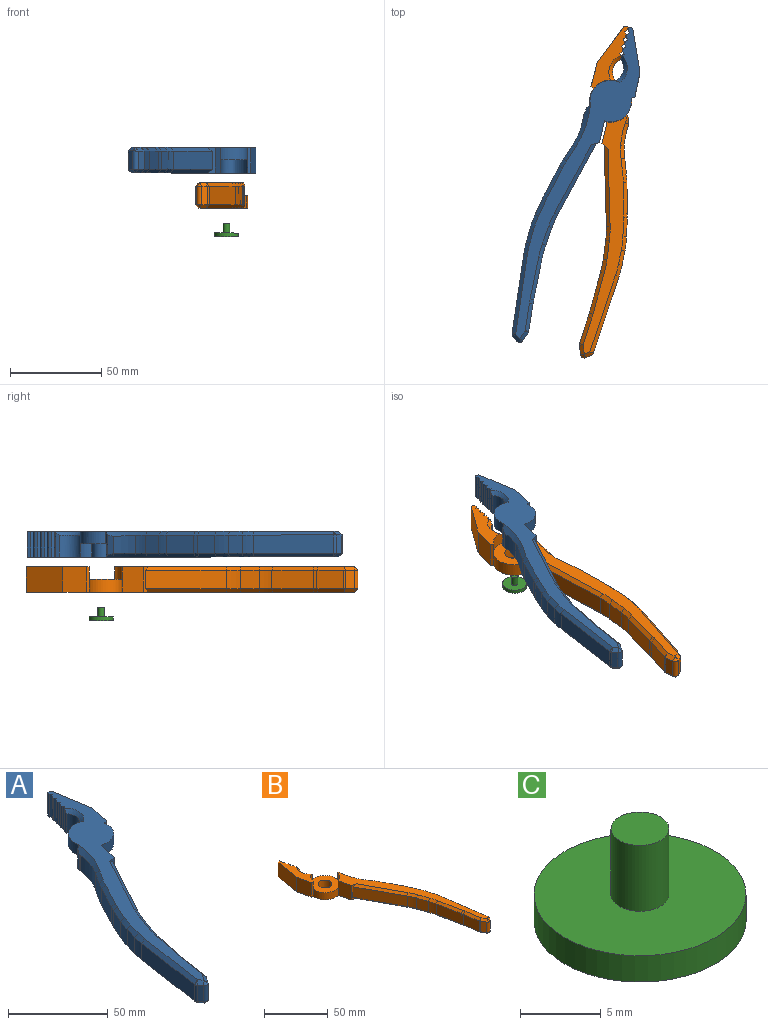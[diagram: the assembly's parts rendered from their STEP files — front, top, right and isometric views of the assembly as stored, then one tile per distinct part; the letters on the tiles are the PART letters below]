
ASSEMBLY  parts=3 mates=3
PART A: 110 faces, bbox 70.2x172.9x14.1 mm
  f0: plane 127.45x48.58mm, normal (0,0,-1), area 866.7mm2, adj f19,f22,f36,f43,f58,f59,f60,f61
  f1: plane 14x1.82mm, normal (-0.97,0.25,0), area 26.3mm2, adj f3,f5,f11,f12
  f2: plane 14x1.29mm, normal (-0.51,0.86,0), area 21mm2, adj f3,f11,f12,f13,f109
  f3: plane 14x1.29mm, normal (-0.86,-0.51,0), area 21mm2, adj f1,f2,f11,f12
  f4: plane 14x1.82mm, normal (-0.97,0.25,0), area 26.3mm2, adj f6,f8,f11,f12
  f5: plane 14x1.29mm, normal (-0.51,0.86,0), area 21mm2, adj f1,f6,f11,f12
  f6: plane 14x1.29mm, normal (-0.86,-0.51,0), area 21mm2, adj f4,f5,f11,f12
  f7: plane 14x1.82mm, normal (-0.97,0.25,0), area 26.3mm2, adj f9,f11,f12,f105
  f8: plane 14x1.29mm, normal (-0.51,0.86,0), area 21mm2, adj f4,f9,f11,f12
  f9: plane 14x1.29mm, normal (-0.86,-0.51,0), area 21mm2, adj f7,f8,f11,f12
  f10: plane 14x1.94mm, normal (-0.97,0.25,0), area 28mm2, adj f11,f12,f41,f106
  f11: plane 170.82x68.11mm, normal (0,0,1), area 1516.7mm2, adj f1,f2,f3,f4,f5,f6,f7,f8
  f12: plane 38.87x13mm, normal (0,0,-1), area 250.2mm2, adj f1,f2,f3,f4,f5,f6,f7,f8
  f13: plane 13.83x2.12mm, normal (-0.97,0.25,0), area 28.2mm2, adj f2,f12,f104,f109
  f14: plane 23.11x22.77mm, normal (0,0,-1), area 337.5mm2, adj f15,f16,f18,f19,f20,f21,f22,f37
  f15: cylinder r=11.39mm len=14.76mm, axis (0,0,1), area 150.8mm2, adj f11,f14,f20,f37
  f16: cylinder r=5.05mm len=10.1mm, axis (0,0,-1), area 234.7mm2, adj f14,f17
  f17: plane 10.1x10.1mm, normal (0,0,-1), area 67.5mm2, adj f16,f44
  f18: cylinder r=11.39mm len=16.38mm, axis (0,0,1), area 154.8mm2, adj f11,f14,f21,f104,f109
  f19: plane 14x11.63mm, normal (0.97,-0.23,0), area 165.9mm2, adj f0,f11,f14,f20,f36,f43
  f20: plane 6.6x0.19mm, normal (0.94,-0.34,0), area 1.3mm2, adj f11,f14,f15,f19
  f21: plane 6.6x0.19mm, normal (-0.35,0.94,0), area 1.3mm2, adj f11,f14,f18,f22,f82
  f22: plane 13.91x1.76mm, normal (-0.47,0.88,0), area 23.7mm2, adj f0,f14,f21,f23,f43,f78,f82
  f23: plane 11.38x3.12mm, normal (-0.9,0.44,0), area 34.7mm2, adj f22,f24,f78,f82
  f24: plane 9.32x0.14mm, normal (-0.99,0.15,0), area 1.3mm2, adj f23,f50,f78,f82
  f25: plane 10x7.38mm, normal (-0.84,0.55,0), area 88.1mm2, adj f49,f51,f79,f83
  f26: plane 14.93x10mm, normal (-0.89,0.46,0), area 168.5mm2, adj f51,f52,f76,f85
  f27: plane 10x9.39mm, normal (-0.91,0.42,0), area 103.4mm2, adj f52,f53,f74,f87
  f28: plane 10x7.47mm, normal (-0.96,0.27,0), area 77.5mm2, adj f53,f54,f72,f89
  f29: plane 43.91x10mm, normal (-0.99,0.15,0), area 443.9mm2, adj f46,f54,f70,f91
  f30: plane 10x2.64mm, normal (-0.78,-0.62,0), area 33.8mm2, adj f46,f47,f68,f93
  f31: plane 10x4.35mm, normal (0.82,-0.57,0), area 53mm2, adj f47,f48,f66,f95
  f32: plane 15.18x10mm, normal (0.99,-0.15,0), area 153.7mm2, adj f48,f55,f64,f97
  f33: plane 22.93x10mm, normal (0.98,-0.2,0), area 233.9mm2, adj f55,f56,f62,f99
  f34: plane 10x9.8mm, normal (0.94,-0.34,0), area 104mm2, adj f56,f57,f60,f101
  f35: plane 39.02x21.16mm, normal (0.88,-0.48,0), area 443.9mm2, adj f36,f57,f58,f103
  f36: plane 14x4.33mm, normal (0.28,-0.96,0), area 29.3mm2, adj f0,f11,f19,f35,f58,f103
  f37: plane 6.6x0.19mm, normal (0.5,-0.87,0), area 1.4mm2, adj f11,f14,f15,f38
  f38: plane 14x1.78mm, normal (0.32,-0.95,0), area 24.8mm2, adj f11,f12,f14,f37,f39,f42
  f39: plane 14x13.16mm, normal (0.98,-0.21,0), area 188.4mm2, adj f11,f12,f38,f40
  f40: plane 24.65x14mm, normal (0.99,0.16,0), area 349.4mm2, adj f11,f12,f39,f41
  f41: plane 14x2.04mm, normal (0.25,0.97,0), area 29.5mm2, adj f10,f11,f12,f40
  f42: cylinder r=11.79mm len=9.67mm, axis (0,0,1), area 101.5mm2, adj f12,f14,f38,f104
  f43: cylinder r=11.79mm len=8.46mm, axis (0,0,1), area 89.9mm2, adj f0,f14,f19,f22
  f44: cylinder r=2mm len=9mm, axis (0,0,-1), area 113.1mm2, adj f17,f45
  f45: plane 4x4mm, normal (0,0,-1), area 12.6mm2, adj f44
  f46: cylinder r=2mm len=10mm, axis (0,0,-1), area 16.4mm2, adj f29,f30,f69,f92
  f47: cylinder r=2mm len=10mm, axis (0,0,-1), area 37.2mm2, adj f30,f31,f67,f94
  f48: cylinder r=2mm len=10mm, axis (0,0,-1), area 9mm2, adj f31,f32,f65,f96
  f49: cylinder r=50mm len=10mm, axis (0,0,1), area 64.9mm2, adj f25,f50,f81,f82
  f50: cylinder r=50mm len=11.8mm, axis (0,0,1), area 118.5mm2, adj f24,f49,f80,f82
  f51: cylinder r=50mm len=10mm, axis (0,0,-1), area 47.7mm2, adj f25,f26,f77,f84
  f52: cylinder r=50mm len=10mm, axis (0,0,-1), area 25.6mm2, adj f26,f27,f75,f86
  f53: cylinder r=50mm len=10mm, axis (0,0,-1), area 79.7mm2, adj f27,f28,f73,f88
  f54: cylinder r=50mm len=10mm, axis (0,0,-1), area 62.4mm2, adj f28,f29,f71,f90
  f55: cylinder r=50mm len=10mm, axis (0,0,1), area 22.1mm2, adj f32,f33,f63,f98
  f56: cylinder r=50mm len=10mm, axis (0,0,1), area 71.2mm2, adj f33,f34,f61,f100
  f57: cylinder r=50mm len=10mm, axis (0,0,1), area 77.5mm2, adj f34,f35,f59,f102
  f58: plane 39.02x22.92mm, normal (0.62,-0.34,-0.71), area 122.7mm2, adj f0,f35,f36,f59
  f59: cone r=52mm half-angle=45deg, axis (0,0,-1), area 22.4mm2, adj f0,f57,f58,f60
  f60: plane 10.47x5.37mm, normal (0.67,-0.24,-0.71), area 29.4mm2, adj f0,f34,f59,f61
  f61: cone r=52mm half-angle=45deg, axis (0,0,-1), area 20.5mm2, adj f0,f56,f60,f62
  f62: plane 23.32x6.6mm, normal (0.69,-0.14,-0.71), area 66.2mm2, adj f0,f33,f61,f63
  f63: cone r=52mm half-angle=45deg, axis (0,0,-1), area 6.4mm2, adj f0,f55,f62,f64
  f64: plane 15.49x4.35mm, normal (0.7,-0.11,-0.71), area 43.5mm2, adj f0,f32,f63,f65
  f65: cone r=2mm half-angle=45deg, axis (0,0,1), area 1.3mm2, adj f48,f64,f66
  f66: plane 5.49x4.67mm, normal (0.58,-0.4,-0.71), area 15mm2, adj f0,f31,f65,f67
  f67: cone r=2mm half-angle=45deg, axis (0,0,1), area 5.3mm2, adj f47,f66,f68
  f68: plane 3.89x3.67mm, normal (-0.55,-0.44,-0.71), area 9.6mm2, adj f0,f30,f67,f69
  f69: cone r=2mm half-angle=45deg, axis (0,0,1), area 2.3mm2, adj f46,f68,f70
  f70: plane 44.21x8.48mm, normal (-0.7,0.1,-0.71), area 125.6mm2, adj f0,f29,f69,f71
  f71: cone r=48mm half-angle=45deg, axis (0,0,1), area 17.3mm2, adj f0,f54,f70,f72
  f72: plane 8.01x4.01mm, normal (-0.68,0.19,-0.71), area 21.9mm2, adj f0,f28,f71,f73
  f73: cone r=48mm half-angle=45deg, axis (0,0,1), area 22.1mm2, adj f0,f53,f72,f74
  f74: plane 10.23x6.14mm, normal (-0.64,0.3,-0.71), area 29.2mm2, adj f0,f27,f73,f75
  f75: cone r=48mm half-angle=45deg, axis (0,0,1), area 7.1mm2, adj f0,f52,f74,f76
  f76: plane 15.86x9.59mm, normal (-0.63,0.33,-0.71), area 47.7mm2, adj f0,f26,f75,f77
  f77: cone r=48mm half-angle=45deg, axis (0,0,1), area 13.2mm2, adj f0,f51,f76,f79
  f78: plane 4.04x2.58mm, normal (-0.7,0.1,-0.71), area 7.7mm2, adj f0,f22,f23,f24,f80
  f79: plane 8.47x6.49mm, normal (-0.59,0.39,-0.71), area 24.9mm2, adj f0,f25,f77,f81
  f80: cone r=52mm half-angle=45deg, axis (0,0,-1), area 35.5mm2, adj f0,f50,f78,f81
  f81: cone r=52mm half-angle=45deg, axis (0,0,-1), area 18.8mm2, adj f0,f49,f79,f80
  f82: cone r=50mm half-angle=45deg, axis (0,0,1), area 72.5mm2, adj f11,f21,f22,f23,f24,f49,f50,f83
  f83: plane 8.47x6.49mm, normal (-0.59,0.39,0.71), area 24.9mm2, adj f11,f25,f82,f84
  f84: cone r=48mm half-angle=45deg, axis (0,0,-1), area 13.2mm2, adj f11,f51,f83,f85
  f85: plane 15.86x9.59mm, normal (-0.63,0.33,0.71), area 47.7mm2, adj f11,f26,f84,f86
  f86: cone r=48mm half-angle=45deg, axis (0,0,-1), area 7.1mm2, adj f11,f52,f85,f87
  f87: plane 10.23x6.14mm, normal (-0.64,0.3,0.71), area 29.2mm2, adj f11,f27,f86,f88
  f88: cone r=48mm half-angle=45deg, axis (0,0,-1), area 22.1mm2, adj f11,f53,f87,f89
  f89: plane 8.01x4.01mm, normal (-0.68,0.19,0.71), area 21.9mm2, adj f11,f28,f88,f90
  f90: cone r=48mm half-angle=45deg, axis (0,0,-1), area 17.3mm2, adj f11,f54,f89,f91
  f91: plane 44.21x8.48mm, normal (-0.7,0.1,0.71), area 125.6mm2, adj f11,f29,f90,f92
  f92: cone r=2mm half-angle=45deg, axis (0,0,-1), area 2.3mm2, adj f46,f91,f93
  f93: plane 3.89x3.67mm, normal (-0.55,-0.44,0.71), area 9.6mm2, adj f11,f30,f92,f94
  f94: cone r=2mm half-angle=45deg, axis (0,0,-1), area 5.3mm2, adj f47,f93,f95
  f95: plane 5.49x4.67mm, normal (0.58,-0.4,0.71), area 15mm2, adj f11,f31,f94,f96
  f96: cone r=2mm half-angle=45deg, axis (0,0,-1), area 1.3mm2, adj f48,f95,f97
  f97: plane 15.49x4.35mm, normal (0.7,-0.11,0.71), area 43.5mm2, adj f11,f32,f96,f98
  f98: cone r=52mm half-angle=45deg, axis (0,0,1), area 6.4mm2, adj f11,f55,f97,f99
  f99: plane 23.32x6.6mm, normal (0.69,-0.14,0.71), area 66.2mm2, adj f11,f33,f98,f100
  f100: cone r=52mm half-angle=45deg, axis (0,0,1), area 20.5mm2, adj f11,f56,f99,f101
  f101: plane 10.47x5.37mm, normal (0.67,-0.24,0.71), area 29.4mm2, adj f11,f34,f100,f102
  f102: cone r=52mm half-angle=45deg, axis (0,0,1), area 22.4mm2, adj f11,f57,f101,f103
  f103: plane 39.02x22.92mm, normal (0.62,-0.34,0.71), area 122.7mm2, adj f11,f35,f36,f102
  f104: cylinder r=7.62mm len=12mm, axis (0,0,1), area 163.4mm2, adj f12,f13,f14,f18,f42,f109
  f105: plane 14x1.29mm, normal (-0.51,0.86,0), area 21mm2, adj f7,f11,f12,f106
  f106: plane 14x1.29mm, normal (-0.86,-0.51,0), area 21mm2, adj f10,f11,f12,f105
  f107: extruded ~7.78x5.87mm, area 30.5mm2, adj f0,f108
  f108: plane 7.97x6.05mm, normal (0,0,-1), area 20.7mm2, adj f107
  f109: cone r=7.62mm half-angle=45deg, axis (0,0,1), area 43.8mm2, adj f2,f11,f13,f18,f104
PART B: 122 faces, bbox 70.1x172.8x14 mm
  f0: plane 170.82x68.11mm, normal (0,0,-1), area 1434.8mm2, adj f1,f2,f3,f4,f5,f6,f7,f8
  f1: plane 14x1.82mm, normal (0.97,0.25,0), area 26.3mm2, adj f0,f2,f6,f24
  f2: plane 14x1.29mm, normal (0.86,-0.51,0), area 21mm2, adj f0,f1,f3,f24
  f3: plane 14x1.29mm, normal (0.51,0.86,0), area 21mm2, adj f0,f2,f11,f24,f121
  f4: plane 14x1.82mm, normal (0.97,0.25,0), area 26.3mm2, adj f0,f5,f9,f24
  f5: plane 14x1.29mm, normal (0.86,-0.51,0), area 21mm2, adj f0,f4,f6,f24
  f6: plane 14x1.29mm, normal (0.51,0.86,0), area 21mm2, adj f0,f1,f5,f24
  f7: plane 14x1.82mm, normal (0.97,0.25,0), area 26.3mm2, adj f0,f8,f24,f108
  f8: plane 14x1.29mm, normal (0.86,-0.51,0), area 21mm2, adj f0,f7,f9,f24
  f9: plane 14x1.29mm, normal (0.51,0.86,0), area 21mm2, adj f0,f4,f8,f24
  f10: plane 14x1.94mm, normal (0.97,0.25,0), area 28mm2, adj f0,f21,f24,f107
  f11: plane 13.83x2.12mm, normal (0.97,0.25,0), area 28.2mm2, adj f0,f3,f104,f121
  f12: cylinder r=11.59mm len=7mm, axis (0,0,-1), area 35.6mm2, adj f0,f13,f103,f105
  f13: plane 23.17x23.17mm, normal (0,0,1), area 328.4mm2, adj f12,f14,f15,f16,f17,f18,f19,f25
  f14: cylinder r=11.59mm len=9.6mm, axis (0,0,-1), area 93.5mm2, adj f13,f20,f24,f104,f121
  f15: cylinder r=11.59mm len=15.03mm, axis (0,0,-1), area 163.4mm2, adj f0,f13,f20,f27
  f16: cylinder r=11.59mm len=9.6mm, axis (0,0,-1), area 96.2mm2, adj f0,f13,f19,f106
  f17: cylinder r=11.59mm len=7mm, axis (0,0,-1), area 30.6mm2, adj f0,f13,f19,f26
  f18: cylinder r=5.45mm len=10.9mm, axis (0,0,-1), area 239.6mm2, adj f0,f13
  f19: plane 7x0mm, normal (0.99,0.14,0), area 0mm2, adj f0,f13,f16,f17
  f20: plane 14x1.78mm, normal (-0.32,-0.95,0), area 26.3mm2, adj f0,f14,f15,f23,f24
  f21: plane 14x2.04mm, normal (-0.25,0.97,0), area 29.5mm2, adj f0,f10,f22,f24
  f22: plane 24.65x14mm, normal (-0.99,0.16,0), area 349.4mm2, adj f0,f21,f23,f24
  f23: plane 14x13.16mm, normal (-0.98,-0.21,0), area 188.4mm2, adj f0,f20,f22,f24
  f24: plane 38.93x10.87mm, normal (0,0,1), area 222.5mm2, adj f1,f2,f3,f4,f5,f6,f7,f8
  f25: cylinder r=11.59mm len=8.36mm, axis (0,0,-1), area 83.9mm2, adj f13,f26,f27,f42
  f26: plane 14x1.74mm, normal (0.47,0.88,0), area 26.4mm2, adj f0,f17,f25,f41,f42,f55,f79
  f27: plane 14x11.63mm, normal (-0.97,-0.23,0), area 167.4mm2, adj f0,f15,f25,f28,f42
  f28: plane 14x4.33mm, normal (-0.28,-0.96,0), area 29.3mm2, adj f0,f27,f29,f42,f78,f102
  f29: plane 39.02x21.16mm, normal (-0.88,-0.48,0), area 443.9mm2, adj f28,f46,f78,f102
  f30: plane 10x9.8mm, normal (-0.94,-0.34,0), area 104mm2, adj f46,f47,f76,f100
  f31: plane 22.93x10mm, normal (-0.98,-0.2,0), area 233.9mm2, adj f47,f48,f74,f98
  f32: plane 15.18x10mm, normal (-0.99,-0.15,0), area 153.7mm2, adj f43,f48,f72,f96
  f33: plane 10x4.35mm, normal (-0.82,-0.57,0), area 53mm2, adj f43,f44,f70,f94
  f34: plane 10x2.64mm, normal (0.78,-0.62,0), area 33.8mm2, adj f44,f45,f68,f92
  f35: plane 43.91x10mm, normal (0.99,0.15,0), area 443.9mm2, adj f45,f49,f66,f90
  f36: plane 10x7.47mm, normal (0.96,0.27,0), area 77.5mm2, adj f49,f50,f64,f88
  f37: plane 10x9.39mm, normal (0.91,0.42,0), area 103.4mm2, adj f50,f51,f62,f86
  f38: plane 14.93x10mm, normal (0.89,0.46,0), area 168.5mm2, adj f51,f52,f60,f84
  f39: plane 10x7.38mm, normal (0.84,0.55,0), area 88.1mm2, adj f52,f54,f58,f82
  f40: plane 10x0.14mm, normal (0.99,0.15,0), area 1.4mm2, adj f41,f53,f55,f79
  f41: plane 12.04x3.03mm, normal (0.9,0.44,0), area 37.2mm2, adj f26,f40,f55,f79
  f42: plane 127.55x48.62mm, normal (0,0,1), area 889.8mm2, adj f25,f26,f27,f28,f55,f56,f57,f58
  f43: cylinder r=2mm len=10mm, axis (0,0,-1), area 9mm2, adj f32,f33,f71,f95
  f44: cylinder r=2mm len=10mm, axis (0,0,-1), area 37.2mm2, adj f33,f34,f69,f93
  f45: cylinder r=2mm len=10mm, axis (0,0,-1), area 16.4mm2, adj f34,f35,f67,f91
  f46: cylinder r=50mm len=10mm, axis (0,0,1), area 77.5mm2, adj f29,f30,f77,f101
  f47: cylinder r=50mm len=10mm, axis (0,0,1), area 71.2mm2, adj f30,f31,f75,f99
  f48: cylinder r=50mm len=10mm, axis (0,0,1), area 22.1mm2, adj f31,f32,f73,f97
  f49: cylinder r=50mm len=10mm, axis (0,0,-1), area 62.4mm2, adj f35,f36,f65,f89
  f50: cylinder r=50mm len=10mm, axis (0,0,-1), area 79.7mm2, adj f36,f37,f63,f87
  f51: cylinder r=50mm len=10mm, axis (0,0,-1), area 25.6mm2, adj f37,f38,f61,f85
  f52: cylinder r=50mm len=10mm, axis (0,0,-1), area 47.7mm2, adj f38,f39,f59,f83
  f53: cylinder r=50mm len=11.8mm, axis (0,0,1), area 122.7mm2, adj f40,f54,f56,f80
  f54: cylinder r=50mm len=10mm, axis (0,0,1), area 64.9mm2, adj f39,f53,f57,f81
  f55: plane 4.04x2.58mm, normal (0.7,0.1,0.71), area 7.7mm2, adj f26,f40,f41,f42,f56
  f56: cone r=52mm half-angle=45deg, axis (0,0,1), area 35.5mm2, adj f42,f53,f55,f57
  f57: cone r=52mm half-angle=45deg, axis (0,0,1), area 18.8mm2, adj f42,f54,f56,f58
  f58: plane 8.47x6.49mm, normal (0.59,0.39,0.71), area 24.9mm2, adj f39,f42,f57,f59
  f59: cone r=48mm half-angle=45deg, axis (0,0,-1), area 13.2mm2, adj f42,f52,f58,f60
  f60: plane 15.86x9.59mm, normal (0.63,0.33,0.71), area 47.7mm2, adj f38,f42,f59,f61
  f61: cone r=48mm half-angle=45deg, axis (0,0,-1), area 7.1mm2, adj f42,f51,f60,f62
  f62: plane 10.23x6.14mm, normal (0.64,0.3,0.71), area 29.2mm2, adj f37,f42,f61,f63
  f63: cone r=48mm half-angle=45deg, axis (0,0,-1), area 22.1mm2, adj f42,f50,f62,f64
  f64: plane 8.01x4.01mm, normal (0.68,0.19,0.71), area 21.9mm2, adj f36,f42,f63,f65
  f65: cone r=48mm half-angle=45deg, axis (0,0,-1), area 17.3mm2, adj f42,f49,f64,f66
  f66: plane 44.21x8.48mm, normal (0.7,0.1,0.71), area 125.6mm2, adj f35,f42,f65,f67
  f67: cone r=2mm half-angle=45deg, axis (0,0,-1), area 2.3mm2, adj f45,f66,f68
  f68: plane 3.89x3.67mm, normal (0.55,-0.44,0.71), area 9.6mm2, adj f34,f42,f67,f69
  f69: cone r=2mm half-angle=45deg, axis (0,0,-1), area 5.3mm2, adj f44,f68,f70
  f70: plane 5.49x4.67mm, normal (-0.58,-0.4,0.71), area 15mm2, adj f33,f42,f69,f71
  f71: cone r=2mm half-angle=45deg, axis (0,0,-1), area 1.3mm2, adj f43,f70,f72
  f72: plane 15.49x4.35mm, normal (-0.7,-0.11,0.71), area 43.5mm2, adj f32,f42,f71,f73
  f73: cone r=52mm half-angle=45deg, axis (0,0,1), area 6.4mm2, adj f42,f48,f72,f74
  f74: plane 23.32x6.6mm, normal (-0.69,-0.14,0.71), area 66.2mm2, adj f31,f42,f73,f75
  f75: cone r=52mm half-angle=45deg, axis (0,0,1), area 20.5mm2, adj f42,f47,f74,f76
  f76: plane 10.47x5.37mm, normal (-0.67,-0.24,0.71), area 29.4mm2, adj f30,f42,f75,f77
  f77: cone r=52mm half-angle=45deg, axis (0,0,1), area 22.4mm2, adj f42,f46,f76,f78
  f78: plane 39.02x22.92mm, normal (-0.62,-0.34,0.71), area 122.7mm2, adj f28,f29,f42,f77
  f79: plane 4.04x2.58mm, normal (0.7,0.1,-0.71), area 7.7mm2, adj f0,f26,f40,f41,f80
  f80: cone r=52mm half-angle=45deg, axis (0,0,-1), area 35.5mm2, adj f0,f53,f79,f81
  f81: cone r=52mm half-angle=45deg, axis (0,0,-1), area 18.8mm2, adj f0,f54,f80,f82
  f82: plane 8.47x6.49mm, normal (0.59,0.39,-0.71), area 24.9mm2, adj f0,f39,f81,f83
  f83: cone r=48mm half-angle=45deg, axis (0,0,1), area 13.2mm2, adj f0,f52,f82,f84
  f84: plane 15.86x9.59mm, normal (0.63,0.33,-0.71), area 47.7mm2, adj f0,f38,f83,f85
  f85: cone r=48mm half-angle=45deg, axis (0,0,1), area 7.1mm2, adj f0,f51,f84,f86
  f86: plane 10.23x6.14mm, normal (0.64,0.3,-0.71), area 29.2mm2, adj f0,f37,f85,f87
  f87: cone r=48mm half-angle=45deg, axis (0,0,1), area 22.1mm2, adj f0,f50,f86,f88
  f88: plane 8.01x4.01mm, normal (0.68,0.19,-0.71), area 21.9mm2, adj f0,f36,f87,f89
  f89: cone r=48mm half-angle=45deg, axis (0,0,1), area 17.3mm2, adj f0,f49,f88,f90
  f90: plane 44.21x8.48mm, normal (0.7,0.1,-0.71), area 125.6mm2, adj f0,f35,f89,f91
  f91: cone r=2mm half-angle=45deg, axis (0,0,1), area 2.3mm2, adj f45,f90,f92
  f92: plane 3.89x3.67mm, normal (0.55,-0.44,-0.71), area 9.6mm2, adj f0,f34,f91,f93
  f93: cone r=2mm half-angle=45deg, axis (0,0,1), area 5.3mm2, adj f44,f92,f94
  f94: plane 5.49x4.67mm, normal (-0.58,-0.4,-0.71), area 15mm2, adj f0,f33,f93,f95
  f95: cone r=2mm half-angle=45deg, axis (0,0,1), area 1.3mm2, adj f43,f94,f96
  f96: plane 15.49x4.35mm, normal (-0.7,-0.11,-0.71), area 43.5mm2, adj f0,f32,f95,f97
  f97: cone r=52mm half-angle=45deg, axis (0,0,-1), area 6.4mm2, adj f0,f48,f96,f98
  f98: plane 23.32x6.6mm, normal (-0.69,-0.14,-0.71), area 66.2mm2, adj f0,f31,f97,f99
  f99: cone r=52mm half-angle=45deg, axis (0,0,-1), area 20.5mm2, adj f0,f47,f98,f100
  f100: plane 10.47x5.37mm, normal (-0.67,-0.24,-0.71), area 29.4mm2, adj f0,f30,f99,f101
  f101: cone r=52mm half-angle=45deg, axis (0,0,-1), area 22.4mm2, adj f0,f46,f100,f102
  f102: plane 39.02x22.92mm, normal (-0.62,-0.34,-0.71), area 122.7mm2, adj f0,f28,f29,f101
  f103: plane 7x0.19mm, normal (-0.97,-0.25,0), area 1.4mm2, adj f0,f12,f13,f104
  f104: cylinder r=7.62mm len=12mm, axis (0,0,1), area 166.4mm2, adj f0,f11,f13,f14,f103,f121
  f105: plane 7x0.19mm, normal (0.97,-0.25,0), area 1.4mm2, adj f0,f12,f13,f106
  f106: cylinder r=7.62mm len=7mm, axis (0,0,1), area 2.3mm2, adj f0,f13,f16,f105
  f107: plane 14x1.29mm, normal (0.86,-0.51,0), area 21mm2, adj f0,f10,f24,f108
  f108: plane 14x1.29mm, normal (0.51,0.86,0), area 21mm2, adj f0,f7,f24,f107
  f109: plane 8.51x1.78mm, normal (-0.98,-0.2,0), area 8.7mm2, adj f0,f110,f119,f120
  f110: plane 1x0.26mm, normal (-1,0,0), area 0.3mm2, adj f0,f109,f111,f120
  f111: plane 1.47x1mm, normal (0,1,0), area 1.5mm2, adj f0,f110,f112,f120
  f112: plane 4x1mm, normal (0.98,0.19,0), area 4.1mm2, adj f0,f111,f113,f120
  f113: plane 4x1mm, normal (-1,0.1,0), area 4mm2, adj f0,f112,f114,f120
  f114: plane 1.91x1mm, normal (0,1,0), area 1.9mm2, adj f0,f113,f115,f120
  f115: plane 8.77x3.16mm, normal (0.94,0.34,0), area 9.3mm2, adj f0,f114,f116,f120
  f116: plane 1.52x1mm, normal (0,-1,0), area 1.5mm2, adj f0,f115,f117,f120
  f117: plane 4.83x2.02mm, normal (-0.92,-0.39,0), area 5.2mm2, adj f0,f116,f118,f120
  f118: plane 4.83x1.08mm, normal (0.98,-0.22,0), area 5mm2, adj f0,f117,f119,f120
  f119: plane 1.32x1mm, normal (0,-1,0), area 1.3mm2, adj f0,f109,f118,f120
  f120: plane 8.77x7.71mm, normal (0,0,-1), area 36.4mm2, adj f109,f110,f111,f112,f113,f114,f115,f116
  f121: cone r=9.62mm half-angle=45deg, axis (0,0,1), area 43mm2, adj f3,f11,f14,f24,f104
PART C: 5 faces, bbox 13.2x13.2x7 mm
  f0: cylinder r=1.8mm len=5mm, axis (0,0,-1), area 56.5mm2, adj f1,f4
  f1: plane 3.6x3.6mm, normal (0,0,1), area 10.2mm2, adj f0
  f2: cylinder r=6.58mm len=13.17mm, axis (0,0,1), area 82.7mm2, adj f3,f4
  f3: plane 13.17x13.17mm, normal (0,0,-1), area 136.2mm2, adj f2
  f4: plane 13.17x13.17mm, normal (0,0,1), area 126mm2, adj f0,f2
PLACE A rot(axis=(0,1,0),0.2deg) t=(-20.2,87.97,-16.2)mm
PLACE B rot(axis=(0,0.01,-1),26.9deg) t=(-12.35,84.44,-35.47)mm
PLACE C rot(axis=(0,1,0),0.2deg) t=(-20.29,87.97,-48.98)mm
MATE cylindrical B.f12 <-> A.f15  axis (0,0,-1) through (-23.68,69.68,-31.94)mm
MATE slider A.f15 <-> C.f0  axis (0,0,-1) through (-23.62,69.68,-11.69)mm
MATE cylindrical B.f12 <-> A.f15  axis (0,0,-1) through (-23.69,69.68,-35.44)mm
